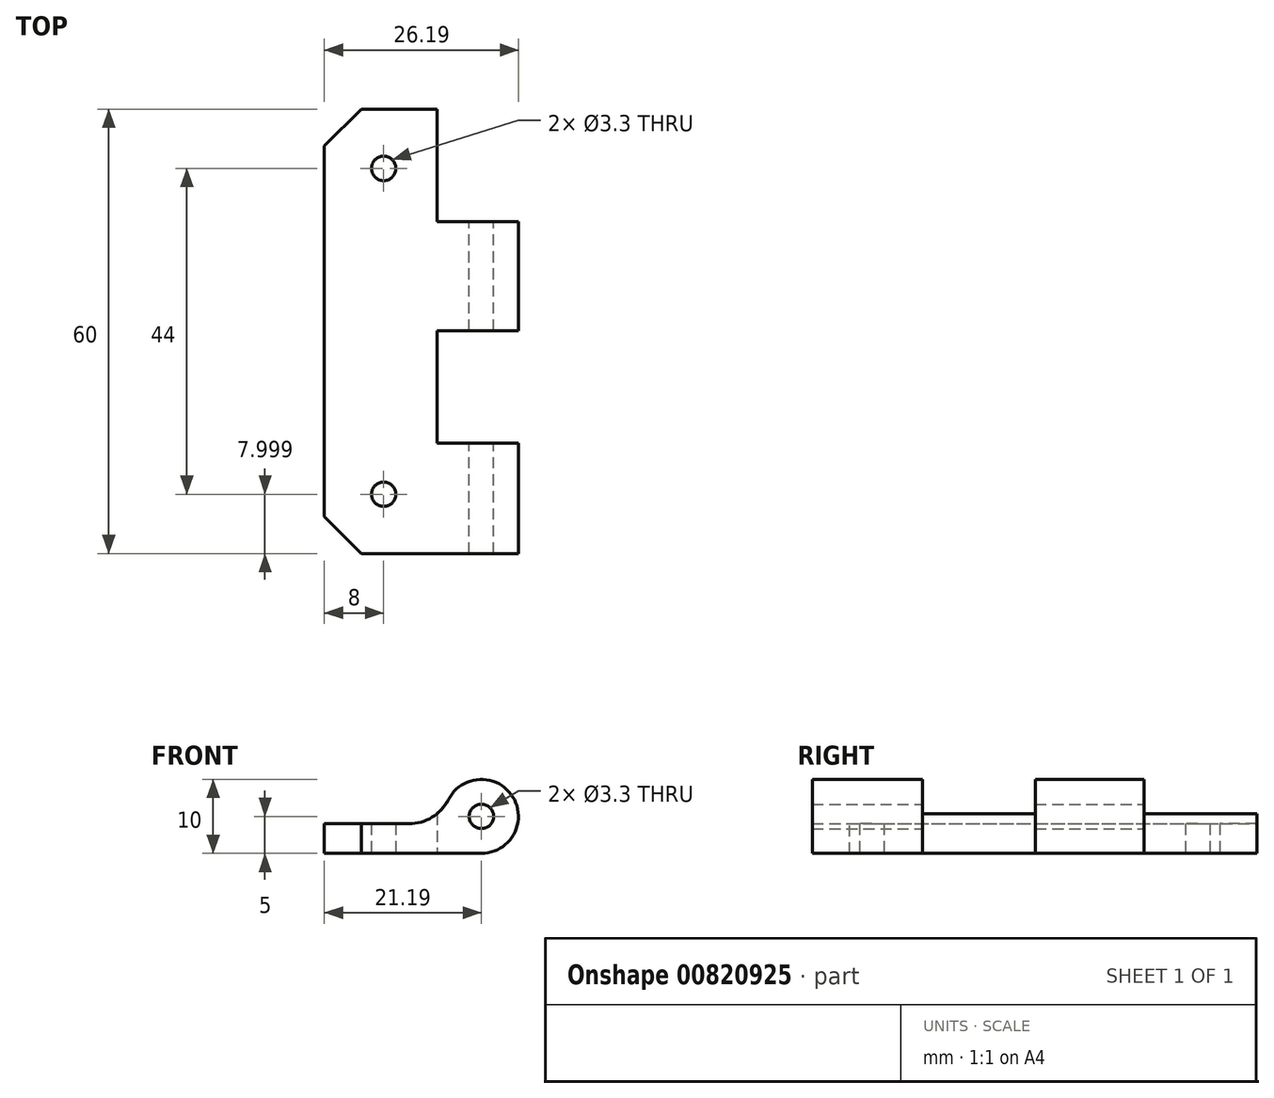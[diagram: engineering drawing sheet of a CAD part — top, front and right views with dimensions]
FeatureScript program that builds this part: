
annotation { "Feature Type Name" : "Feature", "Feature Type Description" : "" }
export const myFeature = defineFeature(function(context is Context, id is Id, definition is map)
    precondition{}
    {
        {
            var Q0;
            Q0=qCreatedBy(makeId("Front.planeOp"),FACE);
            var sketch = newSketch(context, id + "F0", { "sketchPlane" : qUnion([Q0])});
            skLineSegment(sketch, "E0.bottom", {"start": v(0, 0) * mm, "end": v(21.2, 0) * mm});
            skLineSegment(sketch, "E0.top", {"start": v(0, 4) * mm, "end": v(16.3, 4) * mm});
            skLineSegment(sketch, "E0.left", {"start": v(0, 0) * mm, "end": v(0, 4) * mm});
            skArc(sketch, "E1", {"start": v(21.2, 0) * mm, "mid": v(24.35, 8.87) * mm, "end": v(16.3, 4) * mm});
            skCircle(sketch, "E2", {"center": v(21.2, 5) * mm, "radius": 1.65 * mm});
            skPoint(sketch, "E3", {"position": v(26.2, 5) * mm});
            skPoint(sketch, "E4", {"position": v(16.2, 5) * mm});
            skSolve(sketch);
        }
        {
            var Q0;
            Q0 = qSketchRegion(id + "F0", true);
            var Q1;
            Q1 = qSketchRegion(id + "Ffu6EvqpVHtGAEz_1", true);
            extrude(context, id + "F1", {"entities" : qUnion([Q0, Q1]), "depth" : 60 * mm, "offsetDistance" : 25 * mm});
        }
        {
            var Q0;
            Q0=qCreatedBy(makeId("Top.planeOp"),FACE);
            var sketch = newSketch(context, id + "F2", { "sketchPlane" : qUnion([Q0])});
            skPoint(sketch, "E5", {"position": v(8, -8) * mm});
            skPoint(sketch, "E6", {"position": v(8, -52) * mm});
            skSolve(sketch);
        }
        {
            var Q0;
            Q0=sQuery(id+"F2.wireOp",VERTEX,"E5");
            var Q1;
            Q1=sQuery(id+"F2.wireOp",VERTEX,"3f814aa0-051c-435f-9c1c-393610e84903");
            var Q2;
            Q2=sQuery(id+"F2.wireOp",VERTEX,"E6");
            var Q3;
            Q3=makeQuery(id+"F1.opExtrude","SWEPT_BODY",BODY,{"disambiguationData":[OSD([sQuery(id+"F0.wireOp",EDGE,"E0.bottom"),sQuery(id+"F0.wireOp",EDGE,"E0.top"),sQuery(id+"F0.wireOp",EDGE,"E0.left"),sQuery(id+"F0.wireOp",EDGE,"E1"),sQuery(id+"F0.wireOp",EDGE,"4b11f085-5acb-4e5b-92db-e0c4d6ccb226.filletArc")])]});
            hole(context, id + "F3", {"style" : HoleStyle.SIMPLE, "endStyle" : HoleEndStyle.THROUGH, "oppositeDirection" : true, "standardTappedOrClearance" : lookupTablePath({ "standard" : "ISO", "fit" : "Normal", "size" : "M3", "type" : "Clearance" }), "standardBlindInLast" : lookupTablePath({ "fit" : "Standard", "standard" : "ISO", "size" : "M3", "type" : "Clearance" }), "holeDiameter" : 3.3 * mm, "majorDiameter" : 5 * mm, "isTappedThrough" : true, "tappedDepth" : 8 * mm, "tapClearance" : 3, "startFromSketch" : true, "locations" : qUnion([Q0, Q1, Q2]), "scope" : qUnion([Q3])});
        }
        {
            var Q0;
            Q0=qCreatedBy(makeId("Top.planeOp"),FACE);
            var sketch = newSketch(context, id + "F4", { "sketchPlane" : qUnion([Q0])});
            skLineSegment(sketch, "E7.top", {"start": v(15.2, -15.2) * mm, "end": v(26.2, -15.2) * mm});
            skLineSegment(sketch, "E7.right", {"start": v(26.2, 0) * mm, "end": v(26.2, -15.2) * mm});
            skLineSegment(sketch, "E8.bottom", {"start": v(15.2, -29.9) * mm, "end": v(26.2, -29.9) * mm});
            skLineSegment(sketch, "E8.top", {"start": v(15.2, -45.1) * mm, "end": v(26.2, -45.1) * mm});
            skLineSegment(sketch, "E8.left", {"start": v(15.2, -29.9) * mm, "end": v(15.2, -45.1) * mm});
            skLineSegment(sketch, "E8.right", {"start": v(26.2, -29.9) * mm, "end": v(26.2, -45.1) * mm});
            skLineSegment(sketch, "E9", {"start": v(15.2, 0) * mm, "end": v(15.2, -15.2) * mm});
            skLineSegment(sketch, "E10", {"start": v(15.2, 0) * mm, "end": v(26.2, 0) * mm});
            skSolve(sketch);
        }
        {
            var Q0;
            Q0 = qSketchRegion(id + "F4", true);
            extrude(context, id + "F5", {"entities" : qUnion([Q0]), "operationType" : NewBodyOperationType.REMOVE, "endBound" : BoundingType.THROUGH_ALL, "depth" : 25 * mm, "offsetDistance" : 25 * mm});
        }
        {
            var Q0;
            {var subQ0=sQuery(id+"F0.wireOp",EDGE,"E1");var subQ1=sQuery(id+"F0.wireOp",EDGE,"E0.top");Q0=makeQuery(id+"F5.boolean.opBoolean","SPLIT",EDGE,{"disambiguationData":[TD([makeQuery(id+"F5.opExtrude","SWEPT_FACE",FACE,{"disambiguationData":[OSD([sQuery(id+"F4.wireOp",EDGE,"E8.top")])]})])],"derivedFrom":makeQuery(id+"F1.opExtrude","SWEPT_EDGE",EDGE,{"disambiguationData":[OSD([subQ1,subQ0])]})});}
            fillet(context, id + "F6", {"entities" : qUnion([Q0]), "radius" : 6 * mm, "tangentPropagation" : true, "allowEdgeOverflow" : false});
        }
        {
            var Q0;
            Q0=makeQuery(id+"F1.opExtrude","CAP_EDGE",EDGE,{"disambiguationData":[OSD([sQuery(id+"F0.wireOp",EDGE,"E0.left")])],"isStart":false});
            var Q1;
            Q1=makeQuery(id+"F1.opExtrude","CAP_EDGE",EDGE,{"disambiguationData":[OSD([sQuery(id+"F0.wireOp",EDGE,"E0.left")])],"isStart":true});
            chamfer(context, id + "F7", {"entities" : qUnion([Q0, Q1]), "width" : 5 * mm, "tangentPropagation" : true});
        }
    });
